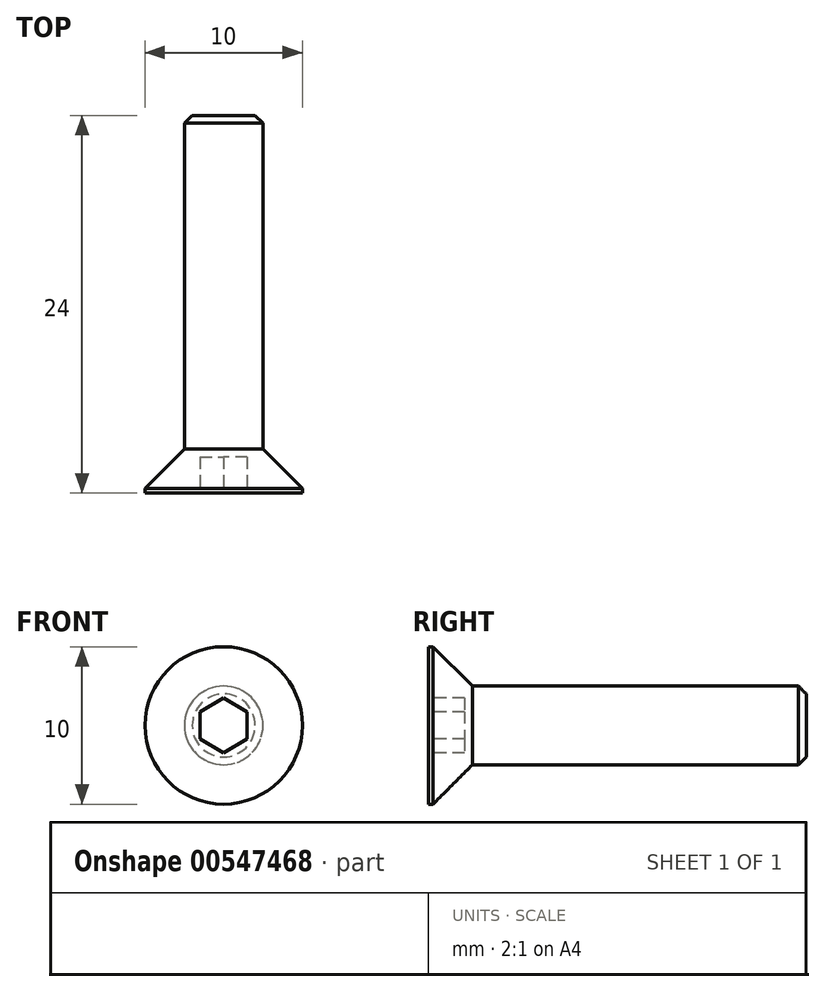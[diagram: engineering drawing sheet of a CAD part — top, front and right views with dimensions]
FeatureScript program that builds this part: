
annotation { "Feature Type Name" : "Feature", "Feature Type Description" : "" }
export const myFeature = defineFeature(function(context is Context, id is Id, definition is map)
    precondition{}
    {
        {
            var Q0;
            Q0=qCreatedBy(makeId("Right.planeOp"),FACE);
            var sketch = newSketch(context, id + "F0", { "sketchPlane" : qUnion([Q0])});
            skLineSegment(sketch, "E0", {"start": v(-2.8, 0) * mm, "end": v(-2.8, 5) * mm});
            skLineSegment(sketch, "E1", {"start": v(-2.8, 5) * mm, "end": v(-2.5, 5) * mm});
            skLineSegment(sketch, "E2", {"start": v(-2.5, 5) * mm, "end": v(0, 2.5) * mm});
            skLineSegment(sketch, "E3", {"start": v(0, 2.5) * mm, "end": v(21.2, 2.5) * mm});
            skLineSegment(sketch, "E4", {"start": v(21.2, 2.5) * mm, "end": v(21.2, 0) * mm});
            skLineSegment(sketch, "E5", {"start": v(-2.8, 0) * mm, "end": v(21.2, 0) * mm});
            skSolve(sketch);
        }
        {
            var Q0;
            Q0=makeQuery(id+"F0.imprint","IMPRINT",FACE,{"disambiguationData":[TD([[makeQuery(id+"F0.imprint","IMPRINT",EDGE,{"derivedFrom":sQuery(id+"F0.wireOp",EDGE,"E0")}),-1.0]])]});
            var Q1;
            Q1=sQuery(id+"F0.wireOp",EDGE,"E5");
            revolve(context, id + "F1", {"entities" : qUnion([Q0]), "axis" : qUnion([Q1]), "revolveType" : RevolveType.FULL});
        }
        {
            var Q0;
            Q0=makeQuery(id+"F1.opRevolve","SWEPT_EDGE",EDGE,{"disambiguationData":[OSD([sQuery(id+"F0.wireOp",EDGE,"E3"),sQuery(id+"F0.wireOp",EDGE,"E4")])]});
            chamfer(context, id + "F2", {"entities" : qUnion([Q0]), "width" : 0.5 * mm, "tangentPropagation" : true});
        }
        {
            var Q0;
            Q0=makeQuery(id+"F1.opRevolve","SWEPT_FACE",FACE,{"disambiguationData":[OSD([sQuery(id+"F0.wireOp",EDGE,"E0")])]});
            var sketch = newSketch(context, id + "F3", { "sketchPlane" : qUnion([Q0])});
            skCircle(sketch, "E6.cCircle", {"center": v(0, 0) * mm, "radius": 1.73 * mm, "construction": true});
            skLineSegment(sketch, "E6.0", {"start": v(1.5, -0.87) * mm, "end": v(0, -1.73) * mm});
            skLineSegment(sketch, "E6.1", {"start": v(0, -1.73) * mm, "end": v(-1.5, -0.87) * mm});
            skLineSegment(sketch, "E6.2", {"start": v(-1.5, -0.87) * mm, "end": v(-1.5, 0.87) * mm});
            skLineSegment(sketch, "E6.3", {"start": v(-1.5, 0.87) * mm, "end": v(0, 1.73) * mm});
            skLineSegment(sketch, "E6.4", {"start": v(0, 1.73) * mm, "end": v(1.5, 0.87) * mm});
            skLineSegment(sketch, "E6.5", {"start": v(1.5, 0.87) * mm, "end": v(1.5, -0.87) * mm});
            skSolve(sketch);
        }
        {
            var Q0;
            Q0=makeQuery(id+"F3.imprint","IMPRINT",FACE,{"disambiguationData":[TD([[makeQuery(id+"F3.imprint","IMPRINT",EDGE,{"derivedFrom":sQuery(id+"F3.wireOp",EDGE,"E6.0")}),-1.0]])]});
            extrude(context, id + "F4", {"entities" : qUnion([Q0]), "operationType" : NewBodyOperationType.REMOVE, "oppositeDirection" : true, "depth" : 2.3 * mm, "offsetDistance" : 25 * mm});
        }
    });
